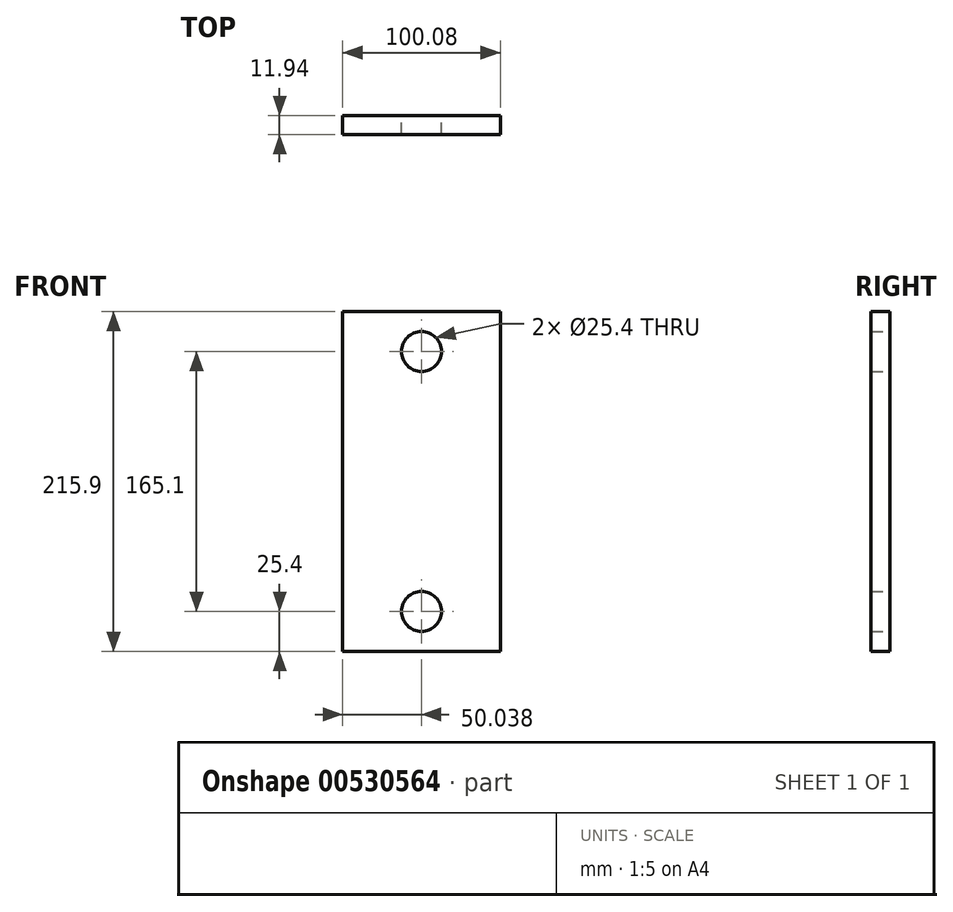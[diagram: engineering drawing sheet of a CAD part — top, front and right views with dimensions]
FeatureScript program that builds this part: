
annotation { "Feature Type Name" : "Feature", "Feature Type Description" : "" }
export const myFeature = defineFeature(function(context is Context, id is Id, definition is map)
    precondition{}
    {
        {
            var Q0;
            Q0=qCreatedBy(makeId("Front.planeOp"),FACE);
            var sketch = newSketch(context, id + "F0", { "sketchPlane" : qUnion([Q0])});
            skLineSegment(sketch, "E0.bottom", {"start": v(0, 0) * mm, "end": v(100.08, 0) * mm});
            skLineSegment(sketch, "E0.top", {"start": v(0, 215.9) * mm, "end": v(100.08, 215.9) * mm});
            skLineSegment(sketch, "E0.left", {"start": v(0, 0) * mm, "end": v(0, 215.9) * mm});
            skLineSegment(sketch, "E0.right", {"start": v(100.08, 0) * mm, "end": v(100.08, 215.9) * mm});
            skCircle(sketch, "E1", {"center": v(50.04, 190.5) * mm, "radius": 12.7 * mm});
            skPoint(sketch, "E1.centerSnap0", {"position": v(50.04, 215.9) * mm});
            skCircle(sketch, "E2", {"center": v(50.04, 25.4) * mm, "radius": 12.7 * mm});
            skPoint(sketch, "E2.centerSnap0", {"position": v(50.04, 0) * mm});
            skSolve(sketch);
        }
        {
            var Q0;
            Q0 = qSketchRegion(id + "F0", true);
            extrude(context, id + "F1", {"entities" : qUnion([Q0]), "depth" : 11.94 * mm, "offsetDistance" : 25.4 * mm});
        }
    });
